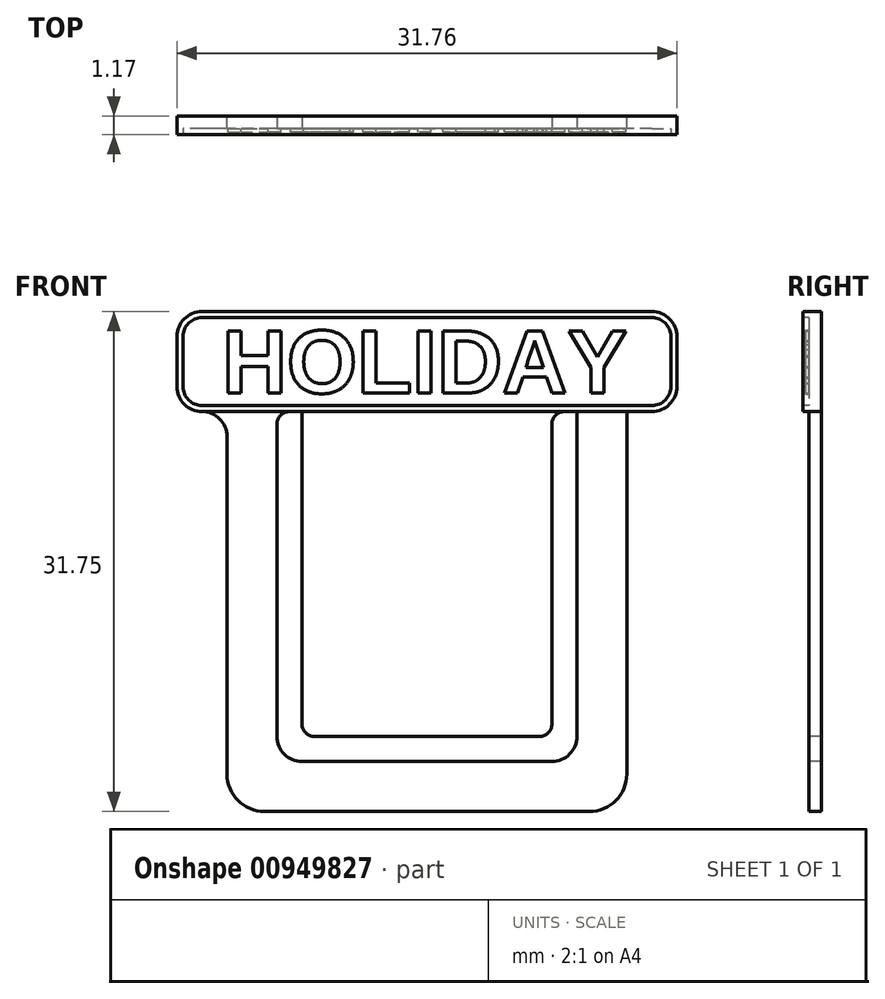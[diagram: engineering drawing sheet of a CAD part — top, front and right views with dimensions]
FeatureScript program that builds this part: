
annotation { "Feature Type Name" : "Feature", "Feature Type Description" : "" }
export const myFeature = defineFeature(function(context is Context, id is Id, definition is map)
    precondition{}
    {
        {
            var Q0;
            Q0=qCreatedBy(makeId("Front.planeOp"),FACE);
            var sketch = newSketch(context, id + "F0", { "sketchPlane" : qUnion([Q0])});
            skLineSegment(sketch, "E0.bottom", {"start": v(12.7, 12.7) * mm, "end": v(-12.7, 12.7) * mm});
            skLineSegment(sketch, "E0.top", {"start": v(12.7, -12.7) * mm, "end": v(-12.7, -12.7) * mm});
            skLineSegment(sketch, "E0.left", {"start": v(12.7, 12.7) * mm, "end": v(12.7, -12.7) * mm});
            skLineSegment(sketch, "E0.right", {"start": v(-12.7, 12.7) * mm, "end": v(-12.7, -12.7) * mm});
            skPoint(sketch, "E0.middle", {"position": v(0, 0) * mm});
            skSolve(sketch);
        }
        {
            var Q0;
            Q0=makeQuery(id+"F0.imprint","IMPRINT",FACE,{"disambiguationData":[TD([[makeQuery(id+"F0.imprint","IMPRINT",EDGE,{"derivedFrom":sQuery(id+"F0.wireOp",EDGE,"E0.bottom")}),1.0]])]});
            extrude(context, id + "F1", {"entities" : qUnion([Q0]), "depth" : 0.8 * mm, "offsetDistance" : 25.4 * mm});
        }
        {
            var Q0;
            Q0=makeQuery(id+"F1.opExtrude","SWEPT_EDGE",EDGE,{"disambiguationData":[OSD([sQuery(id+"F0.wireOp",EDGE,"E0.top"),sQuery(id+"F0.wireOp",EDGE,"E0.left")])]});
            var Q1;
            Q1=makeQuery(id+"F1.opExtrude","SWEPT_EDGE",EDGE,{"disambiguationData":[OSD([sQuery(id+"F0.wireOp",EDGE,"E0.top"),sQuery(id+"F0.wireOp",EDGE,"E0.right")])]});
            fillet(context, id + "F2", {"entities" : qUnion([Q0, Q1]), "radius" : 2.38 * mm, "tangentPropagation" : true, "allowEdgeOverflow" : false});
        }
        {
            var Q0;
            Q0=makeQuery(id+"F1.opExtrude","CAP_FACE",FACE,{"disambiguationData":[OSD([sQuery(id+"F0.wireOp",EDGE,"E0.bottom"),sQuery(id+"F0.wireOp",EDGE,"E0.top"),sQuery(id+"F0.wireOp",EDGE,"E0.left"),sQuery(id+"F0.wireOp",EDGE,"E0.right")])],"isStart":false});
            var sketch = newSketch(context, id + "F3", { "sketchPlane" : qUnion([Q0])});
            skLineSegment(sketch, "E1.bottom", {"start": v(9.52, 12.7) * mm, "end": v(-9.53, 12.7) * mm});
            skLineSegment(sketch, "E1.top", {"start": v(9.53, -9.53) * mm, "end": v(-9.52, -9.53) * mm});
            skLineSegment(sketch, "E1.left", {"start": v(9.52, 12.7) * mm, "end": v(9.53, -9.53) * mm});
            skLineSegment(sketch, "E1.right", {"start": v(-9.53, 12.7) * mm, "end": v(-9.52, -9.53) * mm});
            skPoint(sketch, "E1.middle", {"position": v(0, 0) * mm});
            skSolve(sketch);
        }
        {
            var Q0;
            Q0=makeQuery(id+"F3.imprint","IMPRINT",FACE,{"disambiguationData":[TD([[makeQuery(id+"F3.imprint","IMPRINT",EDGE,{"derivedFrom":sQuery(id+"F3.wireOp",EDGE,"E1.bottom")}),1.0]])]});
            extrude(context, id + "F4", {"entities" : qUnion([Q0]), "operationType" : NewBodyOperationType.REMOVE, "oppositeDirection" : true, "depth" : 4.93 * mm, "offsetDistance" : 25.4 * mm});
        }
        {
            var Q0;
            Q0=makeQuery(id+"F1.opExtrude","CAP_FACE",FACE,{"disambiguationData":[OSD([sQuery(id+"F0.wireOp",EDGE,"E0.bottom"),sQuery(id+"F0.wireOp",EDGE,"E0.top"),sQuery(id+"F0.wireOp",EDGE,"E0.left"),sQuery(id+"F0.wireOp",EDGE,"E0.right")])],"isStart":false});
            var sketch = newSketch(context, id + "F5", { "sketchPlane" : qUnion([Q0])});
            skLineSegment(sketch, "E2.bottom", {"start": v(-15.88, 12.7) * mm, "end": v(15.88, 12.7) * mm});
            skLineSegment(sketch, "E2.top", {"start": v(-15.88, 19.05) * mm, "end": v(15.88, 19.05) * mm});
            skLineSegment(sketch, "E2.left", {"start": v(-15.88, 12.7) * mm, "end": v(-15.88, 19.05) * mm});
            skLineSegment(sketch, "E2.right", {"start": v(15.87, 12.7) * mm, "end": v(15.87, 19.05) * mm});
            skSolve(sketch);
        }
        {
            var Q0;
            Q0=makeQuery(id+"F5.imprint","IMPRINT",FACE,{"disambiguationData":[TD([[makeQuery(id+"F5.imprint","IMPRINT",EDGE,{"derivedFrom":sQuery(id+"F5.wireOp",EDGE,"E2.top")}),-1.0]])]});
            extrude(context, id + "F6", {"entities" : qUnion([Q0]), "operationType" : NewBodyOperationType.ADD, "oppositeDirection" : true, "depth" : 0.8 * mm, "offsetDistance" : 25.4 * mm});
        }
        {
            var Q0;
            Q0=makeQuery(id+"F6.opExtrude","SWEPT_EDGE",EDGE,{"disambiguationData":[OSD([sQuery(id+"F5.wireOp",EDGE,"E2.top"),sQuery(id+"F5.wireOp",EDGE,"E2.left")])]});
            var Q1;
            Q1=makeQuery(id+"F6.opExtrude","SWEPT_EDGE",EDGE,{"disambiguationData":[OSD([sQuery(id+"F5.wireOp",EDGE,"E2.top"),sQuery(id+"F5.wireOp",EDGE,"E2.right")])]});
            var Q2;
            Q2=makeQuery(id+"F6.opExtrude","SWEPT_EDGE",EDGE,{"disambiguationData":[OSD([sQuery(id+"F5.wireOp",EDGE,"E2.bottom"),sQuery(id+"F5.wireOp",EDGE,"E2.right")])]});
            var Q3;
            Q3=makeQuery(id+"F1.opExtrude","SWEPT_EDGE",EDGE,{"disambiguationData":[OSD([sQuery(id+"F0.wireOp",EDGE,"E0.bottom"),sQuery(id+"F0.wireOp",EDGE,"E0.left")])]});
            var Q4;
            Q4=makeQuery(id+"F6.opExtrude","SWEPT_EDGE",EDGE,{"disambiguationData":[OSD([sQuery(id+"F5.wireOp",EDGE,"E2.bottom"),sQuery(id+"F5.wireOp",EDGE,"E2.left")])]});
            var Q5;
            Q5=makeQuery(id+"F1.opExtrude","SWEPT_EDGE",EDGE,{"disambiguationData":[OSD([sQuery(id+"F0.wireOp",EDGE,"E0.bottom"),sQuery(id+"F0.wireOp",EDGE,"E0.right")])]});
            fillet(context, id + "F7", {"entities" : qUnion([Q0, Q1, Q2, Q3, Q4, Q5]), "radius" : 1.59 * mm, "tangentPropagation" : true, "allowEdgeOverflow" : false});
        }
        {
            var Q0;
            Q0=makeQuery(id+"F4.boolean.opBoolean","COPY",EDGE,{"derivedFrom":makeQuery(id+"F4.opExtrude","SWEPT_EDGE",EDGE,{"disambiguationData":[OSD([sQuery(id+"F3.wireOp",EDGE,"E1.top"),sQuery(id+"F3.wireOp",EDGE,"E1.right")])]})});
            var Q1;
            Q1=makeQuery(id+"F4.boolean.opBoolean","COPY",EDGE,{"derivedFrom":makeQuery(id+"F4.opExtrude","SWEPT_EDGE",EDGE,{"disambiguationData":[OSD([sQuery(id+"F3.wireOp",EDGE,"E1.top"),sQuery(id+"F3.wireOp",EDGE,"E1.left")])]})});
            fillet(context, id + "F8", {"entities" : qUnion([Q0, Q1]), "radius" : 1.59 * mm, "tangentPropagation" : true, "allowEdgeOverflow" : false});
        }
        {
            var Q0;
            Q0=makeQuery(id+"F6.boolean.opBoolean","MERGE",FACE,{"derivedFrom":[makeQuery(id+"F1.opExtrude","CAP_FACE",FACE,{"disambiguationData":[OSD([sQuery(id+"F0.wireOp",EDGE,"E0.bottom"),sQuery(id+"F0.wireOp",EDGE,"E0.top"),sQuery(id+"F0.wireOp",EDGE,"E0.left"),sQuery(id+"F0.wireOp",EDGE,"E0.right")])],"isStart":false}),makeQuery(id+"F6.opExtrude","CAP_FACE",FACE,{"disambiguationData":[OSD([sQuery(id+"F5.wireOp",EDGE,"E2.bottom"),sQuery(id+"F5.wireOp",EDGE,"E2.top"),sQuery(id+"F5.wireOp",EDGE,"E2.left"),sQuery(id+"F5.wireOp",EDGE,"E2.right")])],"isStart":true})]});
            var sketch = newSketch(context, id + "F9", { "sketchPlane" : qUnion([Q0])});
            skLineSegment(sketch, "E3.bottom", {"start": v(-7.94, 12.7) * mm, "end": v(7.94, 12.7) * mm});
            skLineSegment(sketch, "E3.top", {"start": v(-7.94, -7.94) * mm, "end": v(7.94, -7.94) * mm});
            skLineSegment(sketch, "E3.left", {"start": v(-7.94, 12.7) * mm, "end": v(-7.94, -7.94) * mm});
            skLineSegment(sketch, "E3.right", {"start": v(7.94, 12.7) * mm, "end": v(7.94, -7.94) * mm});
            skSolve(sketch);
        }
        {
            var Q0;
            Q0=makeQuery(id+"F9.imprint","IMPRINT",FACE,{"disambiguationData":[TD([[makeQuery(id+"F9.imprint","IMPRINT",EDGE,{"derivedFrom":sQuery(id+"F9.wireOp",EDGE,"E3.bottom")}),1.0]])]});
            extrude(context, id + "F10", {"entities" : qUnion([Q0]), "operationType" : NewBodyOperationType.ADD, "oppositeDirection" : true, "depth" : 0.8 * mm, "offsetDistance" : 25.4 * mm});
        }
        {
            var Q0;
            Q0=makeQuery(id+"F10.opExtrude","SWEPT_EDGE",EDGE,{"disambiguationData":[OSD([sQuery(id+"F5.wireOp",EDGE,"E2.bottom"),sQuery(id+"F9.wireOp",EDGE,"E3.bottom"),sQuery(id+"F9.wireOp",EDGE,"E3.left")])]});
            var Q1;
            Q1=makeQuery(id+"F4.boolean.opBoolean","COPY",EDGE,{"derivedFrom":makeQuery(id+"F4.opExtrude","SWEPT_EDGE",EDGE,{"disambiguationData":[OSD([sQuery(id+"F0.wireOp",EDGE,"E0.bottom"),sQuery(id+"F3.wireOp",EDGE,"E1.bottom"),sQuery(id+"F3.wireOp",EDGE,"E1.right")])]})});
            var Q2;
            Q2=makeQuery(id+"F10.opExtrude","SWEPT_EDGE",EDGE,{"disambiguationData":[OSD([sQuery(id+"F5.wireOp",EDGE,"E2.bottom"),sQuery(id+"F9.wireOp",EDGE,"E3.bottom"),sQuery(id+"F9.wireOp",EDGE,"E3.right")])]});
            var Q3;
            Q3=makeQuery(id+"F4.boolean.opBoolean","COPY",EDGE,{"derivedFrom":makeQuery(id+"F4.opExtrude","SWEPT_EDGE",EDGE,{"disambiguationData":[OSD([sQuery(id+"F0.wireOp",EDGE,"E0.bottom"),sQuery(id+"F3.wireOp",EDGE,"E1.bottom"),sQuery(id+"F3.wireOp",EDGE,"E1.left")])]})});
            fillet(context, id + "F11", {"entities" : qUnion([Q0, Q1, Q2, Q3]), "radius" : 0.8 * mm, "tangentPropagation" : true, "allowEdgeOverflow" : false});
        }
        {
            var Q0;
            Q0=makeQuery(id+"F10.opExtrude","SWEPT_EDGE",EDGE,{"disambiguationData":[OSD([sQuery(id+"F9.wireOp",EDGE,"E3.top"),sQuery(id+"F9.wireOp",EDGE,"E3.left")])]});
            var Q1;
            Q1=makeQuery(id+"F10.opExtrude","SWEPT_EDGE",EDGE,{"disambiguationData":[OSD([sQuery(id+"F9.wireOp",EDGE,"E3.top"),sQuery(id+"F9.wireOp",EDGE,"E3.right")])]});
            fillet(context, id + "F12", {"entities" : qUnion([Q0, Q1]), "radius" : 0.8 * mm, "tangentPropagation" : true, "allowEdgeOverflow" : false});
        }
        {
            var Q0;
            Q0=makeQuery(id+"F10.boolean.opBoolean","MERGE",FACE,{"derivedFrom":[makeQuery(id+"F6.boolean.opBoolean","MERGE",FACE,{"derivedFrom":[makeQuery(id+"F1.opExtrude","CAP_FACE",FACE,{"disambiguationData":[OSD([sQuery(id+"F0.wireOp",EDGE,"E0.bottom"),sQuery(id+"F0.wireOp",EDGE,"E0.top"),sQuery(id+"F0.wireOp",EDGE,"E0.left"),sQuery(id+"F0.wireOp",EDGE,"E0.right")])],"isStart":false}),makeQuery(id+"F6.opExtrude","CAP_FACE",FACE,{"disambiguationData":[OSD([sQuery(id+"F5.wireOp",EDGE,"E2.bottom"),sQuery(id+"F5.wireOp",EDGE,"E2.top"),sQuery(id+"F5.wireOp",EDGE,"E2.left"),sQuery(id+"F5.wireOp",EDGE,"E2.right")])],"isStart":true})]}),makeQuery(id+"F10.opExtrude","CAP_FACE",FACE,{"disambiguationData":[OSD([sQuery(id+"F9.wireOp",EDGE,"E3.bottom"),sQuery(id+"F9.wireOp",EDGE,"E3.top"),sQuery(id+"F9.wireOp",EDGE,"E3.left"),sQuery(id+"F9.wireOp",EDGE,"E3.right")])],"isStart":true})]});
            var sketch = newSketch(context, id + "F13", { "sketchPlane" : qUnion([Q0])});
            skArc(sketch, "E4.0", {"start": v(-14.29, 19.05) * mm, "mid": v(-15.41, 18.59) * mm, "end": v(-15.88, 17.46) * mm});
            skLineSegment(sketch, "E5.0", {"start": v(-15.88, 14.29) * mm, "end": v(-15.88, 17.46) * mm});
            skArc(sketch, "E6.0", {"start": v(-15.88, 14.29) * mm, "mid": v(-15.41, 13.16) * mm, "end": v(-14.29, 12.7) * mm});
            skLineSegment(sketch, "E7.0", {"start": v(-14.29, 19.05) * mm, "end": v(14.29, 19.05) * mm});
            skArc(sketch, "E8.0", {"start": v(15.87, 17.46) * mm, "mid": v(15.41, 18.59) * mm, "end": v(14.29, 19.05) * mm});
            skLineSegment(sketch, "E9.0", {"start": v(15.87, 14.29) * mm, "end": v(15.87, 17.46) * mm});
            skArc(sketch, "E10.0", {"start": v(14.29, 12.7) * mm, "mid": v(15.41, 13.16) * mm, "end": v(15.87, 14.29) * mm});
            skLineSegment(sketch, "E11", {"start": v(-14.29, 12.7) * mm, "end": v(14.29, 12.7) * mm});
            skSolve(sketch);
        }
        {
            var Q0;
            Q0=makeQuery(id+"F13.imprint","IMPRINT",FACE,{"disambiguationData":[TD([[makeQuery(id+"F13.imprint","IMPRINT",EDGE,{"derivedFrom":sQuery(id+"F13.wireOp",EDGE,"E4.0")}),1.0]])]});
            extrude(context, id + "F14", {"entities" : qUnion([Q0]), "operationType" : NewBodyOperationType.ADD, "depth" : 0.38 * mm, "offsetDistance" : 25.4 * mm});
        }
        {
            var Q0;
            Q0=makeQuery(id+"F14.opExtrude","CAP_FACE",FACE,{"disambiguationData":[OSD([sQuery(id+"F13.wireOp",EDGE,"E4.0"),sQuery(id+"F13.wireOp",EDGE,"E5.0"),sQuery(id+"F13.wireOp",EDGE,"E6.0"),sQuery(id+"F13.wireOp",EDGE,"E7.0"),sQuery(id+"F13.wireOp",EDGE,"E8.0"),sQuery(id+"F13.wireOp",EDGE,"E9.0"),sQuery(id+"F13.wireOp",EDGE,"E10.0"),sQuery(id+"F13.wireOp",EDGE,"E11")])],"isStart":false});
            var sketch = newSketch(context, id + "F15", { "sketchPlane" : qUnion([Q0])});
            skArc(sketch, "E12.0", {"start": v(-14.29, 19.05) * mm, "mid": v(-15.41, 18.59) * mm, "end": v(-15.88, 17.46) * mm});
            skLineSegment(sketch, "E13.0", {"start": v(-14.29, 19.05) * mm, "end": v(14.29, 19.05) * mm});
            skLineSegment(sketch, "E14.0", {"start": v(-15.88, 14.29) * mm, "end": v(-15.88, 17.46) * mm});
            skArc(sketch, "E15.0", {"start": v(-15.88, 14.29) * mm, "mid": v(-15.41, 13.16) * mm, "end": v(-14.29, 12.7) * mm});
            skLineSegment(sketch, "E16.0", {"start": v(-14.29, 12.7) * mm, "end": v(14.29, 12.7) * mm});
            skArc(sketch, "E17.0", {"start": v(14.29, 12.7) * mm, "mid": v(15.41, 13.16) * mm, "end": v(15.87, 14.29) * mm});
            skArc(sketch, "E18.0", {"start": v(15.87, 17.46) * mm, "mid": v(15.41, 18.59) * mm, "end": v(14.29, 19.05) * mm});
            skArc(sketch, "E19", {"start": v(-14.29, 18.67) * mm, "mid": v(-15.14, 18.32) * mm, "end": v(-15.5, 17.46) * mm});
            skArc(sketch, "E20", {"start": v(-15.5, 14.29) * mm, "mid": v(-15.14, 13.43) * mm, "end": v(-14.29, 13.08) * mm});
            skArc(sketch, "E21", {"start": v(15.5, 17.46) * mm, "mid": v(15.14, 18.32) * mm, "end": v(14.29, 18.67) * mm});
            skArc(sketch, "E22", {"start": v(14.29, 13.08) * mm, "mid": v(15.14, 13.43) * mm, "end": v(15.5, 14.29) * mm});
            skLineSegment(sketch, "E23", {"start": v(-14.29, 19.05) * mm, "end": v(-14.29, 12.7) * mm, "construction": true});
            skLineSegment(sketch, "E24", {"start": v(-15.88, 17.46) * mm, "end": v(15.87, 17.46) * mm, "construction": true});
            skLineSegment(sketch, "E25", {"start": v(14.29, 19.05) * mm, "end": v(14.29, 12.7) * mm, "construction": true});
            skLineSegment(sketch, "E26", {"start": v(15.87, 14.29) * mm, "end": v(-15.88, 14.29) * mm, "construction": true});
            skLineSegment(sketch, "E27", {"start": v(14.29, 18.67) * mm, "end": v(-14.29, 18.67) * mm});
            skLineSegment(sketch, "E28", {"start": v(-15.5, 17.46) * mm, "end": v(-15.5, 14.29) * mm});
            skLineSegment(sketch, "E29", {"start": v(-14.29, 13.08) * mm, "end": v(14.29, 13.08) * mm});
            skLineSegment(sketch, "E30", {"start": v(15.5, 17.46) * mm, "end": v(15.5, 14.29) * mm});
            skSolve(sketch);
        }
        {
            var Q0;
            Q0=makeQuery(id+"F15.imprint","IMPRINT",FACE,{"disambiguationData":[TD([[makeQuery(id+"F15.imprint","IMPRINT",EDGE,{"derivedFrom":sQuery(id+"F15.wireOp",EDGE,"E19")}),1.0]])]});
            var Q1;
            {var subQ0=sQuery(id+"F9.wireOp",EDGE,"E3.right");var subQ1=sQuery(id+"F9.wireOp",EDGE,"E3.top");var subQ3=sQuery(id+"F0.wireOp",EDGE,"E0.bottom");var subQ4=sQuery(id+"F9.wireOp",EDGE,"E3.left");var subQ5=makeQuery(id+"F6.opExtrude","CAP_FACE",FACE,{"disambiguationData":[OSD([sQuery(id+"F5.wireOp",EDGE,"E2.bottom"),sQuery(id+"F5.wireOp",EDGE,"E2.top"),sQuery(id+"F5.wireOp",EDGE,"E2.left"),sQuery(id+"F5.wireOp",EDGE,"E2.right")])],"isStart":true});var subQ6=makeQuery(id+"F1.opExtrude","CAP_FACE",FACE,{"disambiguationData":[OSD([subQ3,sQuery(id+"F0.wireOp",EDGE,"E0.top"),sQuery(id+"F0.wireOp",EDGE,"E0.left"),sQuery(id+"F0.wireOp",EDGE,"E0.right")])],"isStart":false});var subQ7=makeQuery(id+"F10.opExtrude","CAP_FACE",FACE,{"disambiguationData":[OSD([sQuery(id+"F9.wireOp",EDGE,"E3.bottom"),subQ1,subQ4,subQ0])],"isStart":true});Q1=makeQuery(id+"F14.boolean.opBoolean","SPLIT",FACE,{"disambiguationData":[TD([makeQuery(id+"F10.opExtrude","SWEPT_FACE",FACE,{"disambiguationData":[OSD([subQ1])]})])],"derivedFrom":makeQuery(id+"F10.boolean.opBoolean","MERGE",FACE,{"derivedFrom":[makeQuery(id+"F6.boolean.opBoolean","MERGE",FACE,{"derivedFrom":[subQ6,subQ5]}),subQ7]})});}
            extrude(context, id + "F16", {"entities" : qUnion([Q0]), "operationType" : NewBodyOperationType.REMOVE, "endBound" : BoundingType.UP_TO_SURFACE, "oppositeDirection" : true, "depth" : 25.4 * mm, "endBoundEntityFace" : qUnion([Q1]), "offsetDistance" : 25.4 * mm});
        }
        {
            var Q0;
            Q0=qCreatedBy(makeId("Front.planeOp"),FACE);
            var sketch = newSketch(context, id + "F17", { "sketchPlane" : qUnion([Q0])});
            skText(sketch, "E31", { "text": "HOLIDAY", "fontName": "Arimo-Bold.ttf"});
            const initialGuessF17  = {"E31": [-0.01302, 0.01388, 1, 0, 0.00412]};
            skSetInitialGuess(sketch, initialGuessF17);
            skSolve(sketch);
        }
        {
            var Q0;
            Q0=qSketchRegion(id+"F17",true);
            extrude(context, id + "F18", {"entities" : qUnion([Q0]), "operationType" : NewBodyOperationType.ADD, "depth" : 1.02 * mm, "offsetDistance" : 25.4 * mm});
        }
    });
